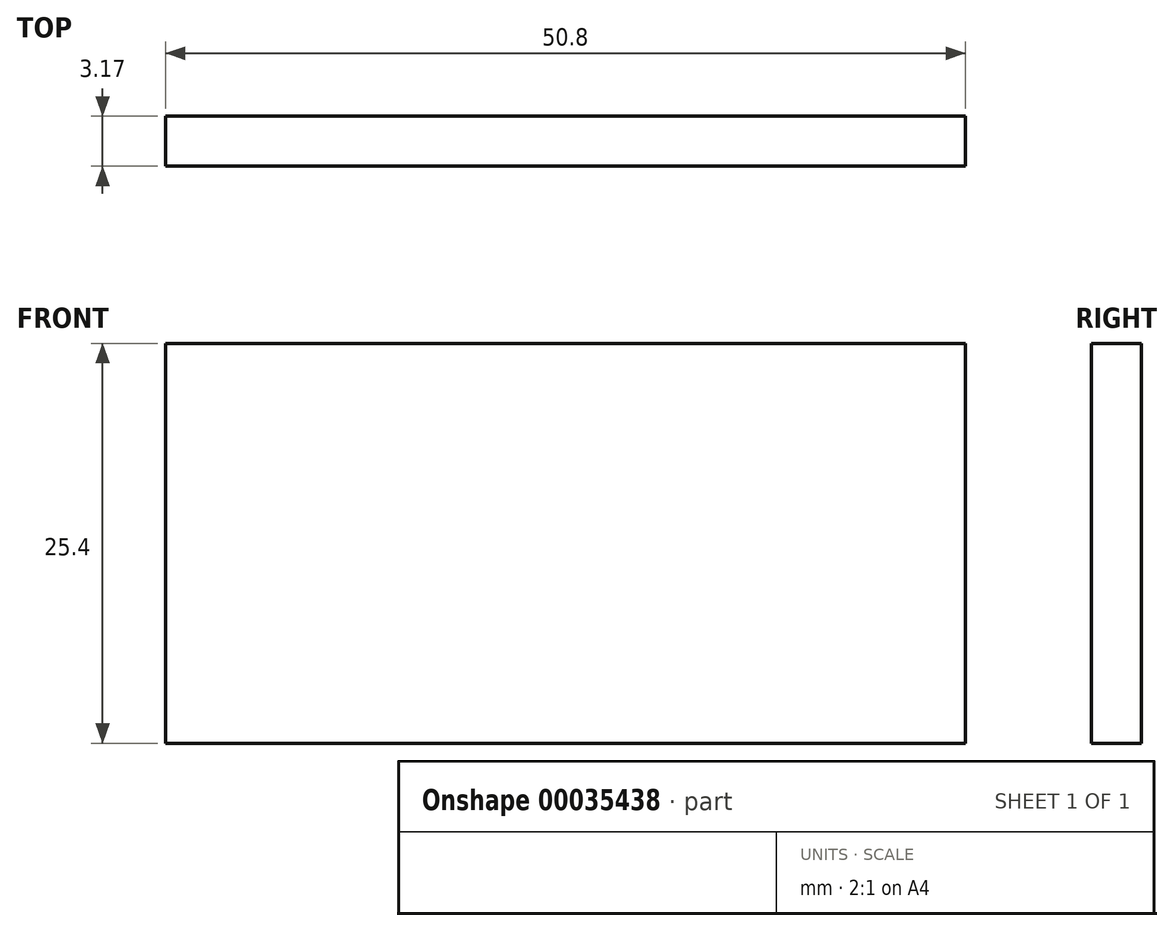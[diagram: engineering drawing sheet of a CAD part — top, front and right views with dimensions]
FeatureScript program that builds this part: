
annotation { "Feature Type Name" : "Feature", "Feature Type Description" : "" }
export const myFeature = defineFeature(function(context is Context, id is Id, definition is map)
    precondition{}
    {
        {
            var Q0;
            Q0=qCreatedBy(makeId("Front.planeOp"),FACE);
            var sketch = newSketch(context, id + "F0", { "sketchPlane" : qUnion([Q0])});
            skLineSegment(sketch, "E0.rect.bottom", {"start": v(25.4, -12.7) * mm, "end": v(-25.4, -12.7) * mm});
            skLineSegment(sketch, "E0.rect.top", {"start": v(25.4, 12.7) * mm, "end": v(-25.4, 12.7) * mm});
            skLineSegment(sketch, "E0.rect.left", {"start": v(25.4, -12.7) * mm, "end": v(25.4, 12.7) * mm});
            skLineSegment(sketch, "E0.rect.right", {"start": v(-25.4, -12.7) * mm, "end": v(-25.4, 12.7) * mm});
            skPoint(sketch, "E0.rect.middle", {"position": v(0, 0) * mm});
            skSolve(sketch);
        }
        {
            var Q0;
            Q0=makeQuery(id+"F0.imprint","IMPRINT",FACE,{"disambiguationData":[TD([[makeQuery(id+"F0.imprint","IMPRINT",EDGE,{"derivedFrom":sQuery(id+"F0.wireOp",EDGE,"E0.rect.bottom")}),-1.0]])]});
            extrude(context, id + "F1", {"entities" : qUnion([Q0]), "depth" : 3.17 * mm});
        }
    });
